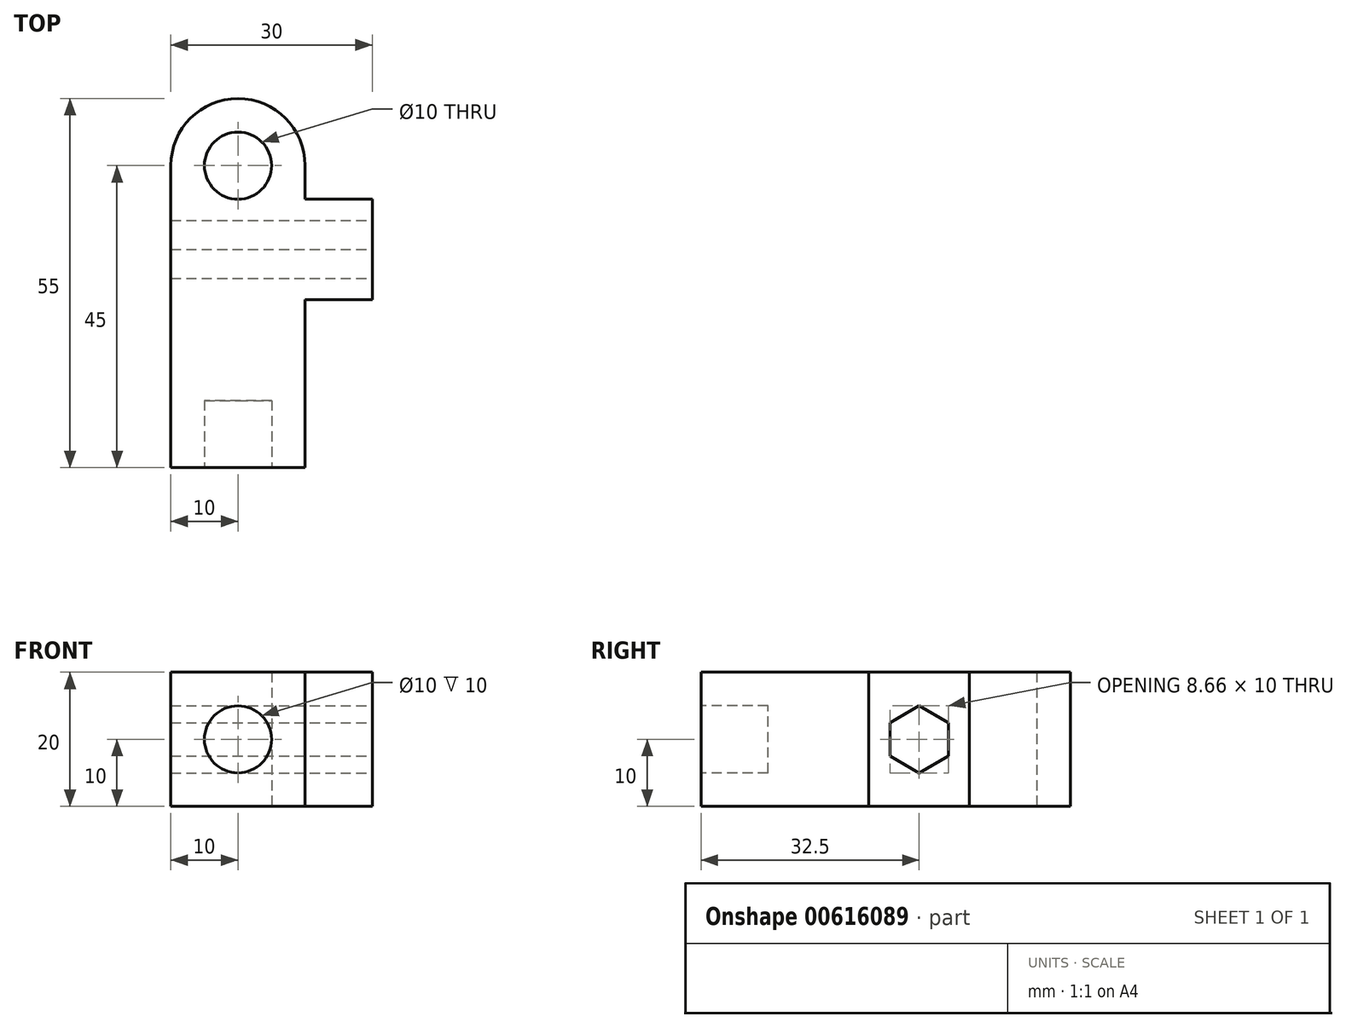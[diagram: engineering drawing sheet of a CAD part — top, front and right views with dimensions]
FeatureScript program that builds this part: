
annotation { "Feature Type Name" : "Feature", "Feature Type Description" : "" }
export const myFeature = defineFeature(function(context is Context, id is Id, definition is map)
    precondition{}
    {
        {
            var Q0;
            Q0=qCreatedBy(makeId("Top.planeOp"),FACE);
            var sketch = newSketch(context, id + "F0", { "sketchPlane" : qUnion([Q0])});
            skLineSegment(sketch, "E0.bottom", {"start": v(0, 0) * mm, "end": v(20, 0) * mm});
            skLineSegment(sketch, "E0.left", {"start": v(0, 0) * mm, "end": v(0, 45) * mm});
            skLineSegment(sketch, "E0.right", {"start": v(20, 0) * mm, "end": v(20, 45) * mm});
            skArc(sketch, "E1", {"start": v(20, 45) * mm, "mid": v(10, 55) * mm, "end": v(0, 45) * mm});
            skCircle(sketch, "E2", {"center": v(10, 45) * mm, "radius": 5 * mm});
            skSolve(sketch);
        }
        {
            var Q0;
            Q0 = qSketchRegion(id + "F0", true);
            extrude(context, id + "F1", {"entities" : qUnion([Q0]), "depth" : 20 * mm, "offsetDistance" : 25 * mm});
        }
        {
            var Q0;
            Q0=makeQuery(id+"F1.opExtrude","SWEPT_FACE",FACE,{"disambiguationData":[OSD([sQuery(id+"F0.wireOp",EDGE,"E0.bottom")])]});
            var sketch = newSketch(context, id + "F2", { "sketchPlane" : qUnion([Q0])});
            skCircle(sketch, "E3", {"center": v(10, 10) * mm, "radius": 5 * mm});
            skPoint(sketch, "E3.centerSnap0", {"position": v(10, 20) * mm});
            skPoint(sketch, "E3.centerSnap1", {"position": v(0, 10) * mm});
            skSolve(sketch);
        }
        {
            var Q0;
            Q0 = qSketchRegion(id + "F2", true);
            extrude(context, id + "F3", {"entities" : qUnion([Q0]), "operationType" : NewBodyOperationType.REMOVE, "oppositeDirection" : true, "depth" : 10 * mm, "offsetDistance" : 25 * mm});
        }
        {
            var Q0;
            Q0=makeQuery(id+"F1.opExtrude","SWEPT_FACE",FACE,{"disambiguationData":[OSD([sQuery(id+"F0.wireOp",EDGE,"E0.right")])]});
            var sketch = newSketch(context, id + "F4", { "sketchPlane" : qUnion([Q0])});
            skLineSegment(sketch, "E4.bottom", {"start": v(25, 20) * mm, "end": v(40, 20) * mm});
            skLineSegment(sketch, "E4.top", {"start": v(25, 0) * mm, "end": v(40, 0) * mm});
            skLineSegment(sketch, "E4.left", {"start": v(25, 20) * mm, "end": v(25, 0) * mm});
            skLineSegment(sketch, "E4.right", {"start": v(40, 20) * mm, "end": v(40, 0) * mm});
            skSolve(sketch);
        }
        {
            var Q0;
            Q0 = qSketchRegion(id + "F4", true);
            extrude(context, id + "F5", {"entities" : qUnion([Q0]), "operationType" : NewBodyOperationType.ADD, "depth" : 10 * mm, "offsetDistance" : 25 * mm});
        }
        {
            var Q0;
            Q0=makeQuery(id+"F5.opExtrude","CAP_FACE",FACE,{"disambiguationData":[OSD([sQuery(id+"F4.wireOp",EDGE,"E4.bottom"),sQuery(id+"F4.wireOp",EDGE,"E4.top"),sQuery(id+"F4.wireOp",EDGE,"E4.left"),sQuery(id+"F4.wireOp",EDGE,"E4.right")])],"isStart":false});
            var sketch = newSketch(context, id + "F6", { "sketchPlane" : qUnion([Q0])});
            skCircle(sketch, "E5.cCircle", {"center": v(32.5, 10) * mm, "radius": 4.33 * mm, "construction": true});
            skPoint(sketch, "E5.cCircle.centerSnap0", {"position": v(25, 10) * mm});
            skPoint(sketch, "E5.cCircle.centerSnap1", {"position": v(32.5, 20) * mm});
            skLineSegment(sketch, "E5.0", {"start": v(32.5, 15) * mm, "end": v(36.83, 12.5) * mm});
            skLineSegment(sketch, "E5.1", {"start": v(36.83, 12.5) * mm, "end": v(36.83, 7.5) * mm});
            skLineSegment(sketch, "E5.2", {"start": v(36.83, 7.5) * mm, "end": v(32.5, 5) * mm});
            skLineSegment(sketch, "E5.3", {"start": v(32.5, 5) * mm, "end": v(28.17, 7.5) * mm});
            skLineSegment(sketch, "E5.4", {"start": v(28.17, 7.5) * mm, "end": v(28.17, 12.5) * mm});
            skLineSegment(sketch, "E5.5", {"start": v(28.17, 12.5) * mm, "end": v(32.5, 15) * mm});
            skPoint(sketch, "E5.0.midPoint", {"position": v(34.67, 13.75) * mm});
            skSolve(sketch);
        }
        {
            var Q0;
            Q0 = qSketchRegion(id + "F6", true);
            extrude(context, id + "F7", {"entities" : qUnion([Q0]), "operationType" : NewBodyOperationType.REMOVE, "endBound" : BoundingType.UP_TO_NEXT, "oppositeDirection" : true, "depth" : 25 * mm, "offsetDistance" : 25 * mm});
        }
    });
